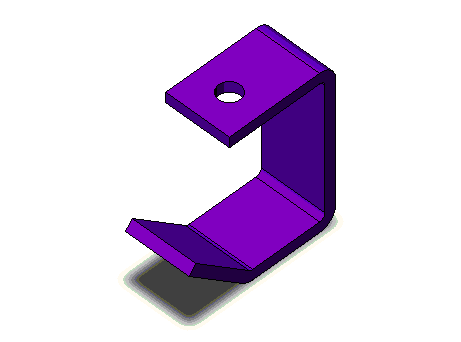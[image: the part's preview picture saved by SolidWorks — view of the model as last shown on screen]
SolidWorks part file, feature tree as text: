
SOLIDWORKS PART (.sldprt)
format: sldprt  version: not decoded by parser v0  size: 142,336 bytes
history: native  units: mm
features: sketch x2, fillet x2, material x1, extrude x1, shell x1, cut_extrude x1 (+14 scaffold rows collapsed)
feature tree (22):
  scaffold x14  (default folders/planes/origin — collapsed)
  material  "Material <sin especificar>"
  sketch  "Sketch1"  dims[D1=40.0deg D2=82.55mm D3=44.45mm D4=~42.763804mm D5=57.15mm]
  extrude  "Boss-Extrude1"  Depth=38.1mm
  shell  "Shell1"  Thickness=6.35mm
  fillet  "Fillet1"  Radius=3.175mm
  fillet  "Fillet2"  Radius=9.525mm
  sketch  "Sketch2"  dims[D1=12.7mm D2=19.05mm]
  cut_extrude  "Cut-Extrude1"  [1 undecoded]
decode coverage: 6 of 7 modeling features carry decoded parameters
note: ~ marks probable driven/reference dimensions
note: 1 parameter value undecoded
note: suppression state not decoded; provenance and decode notes live in map.json
